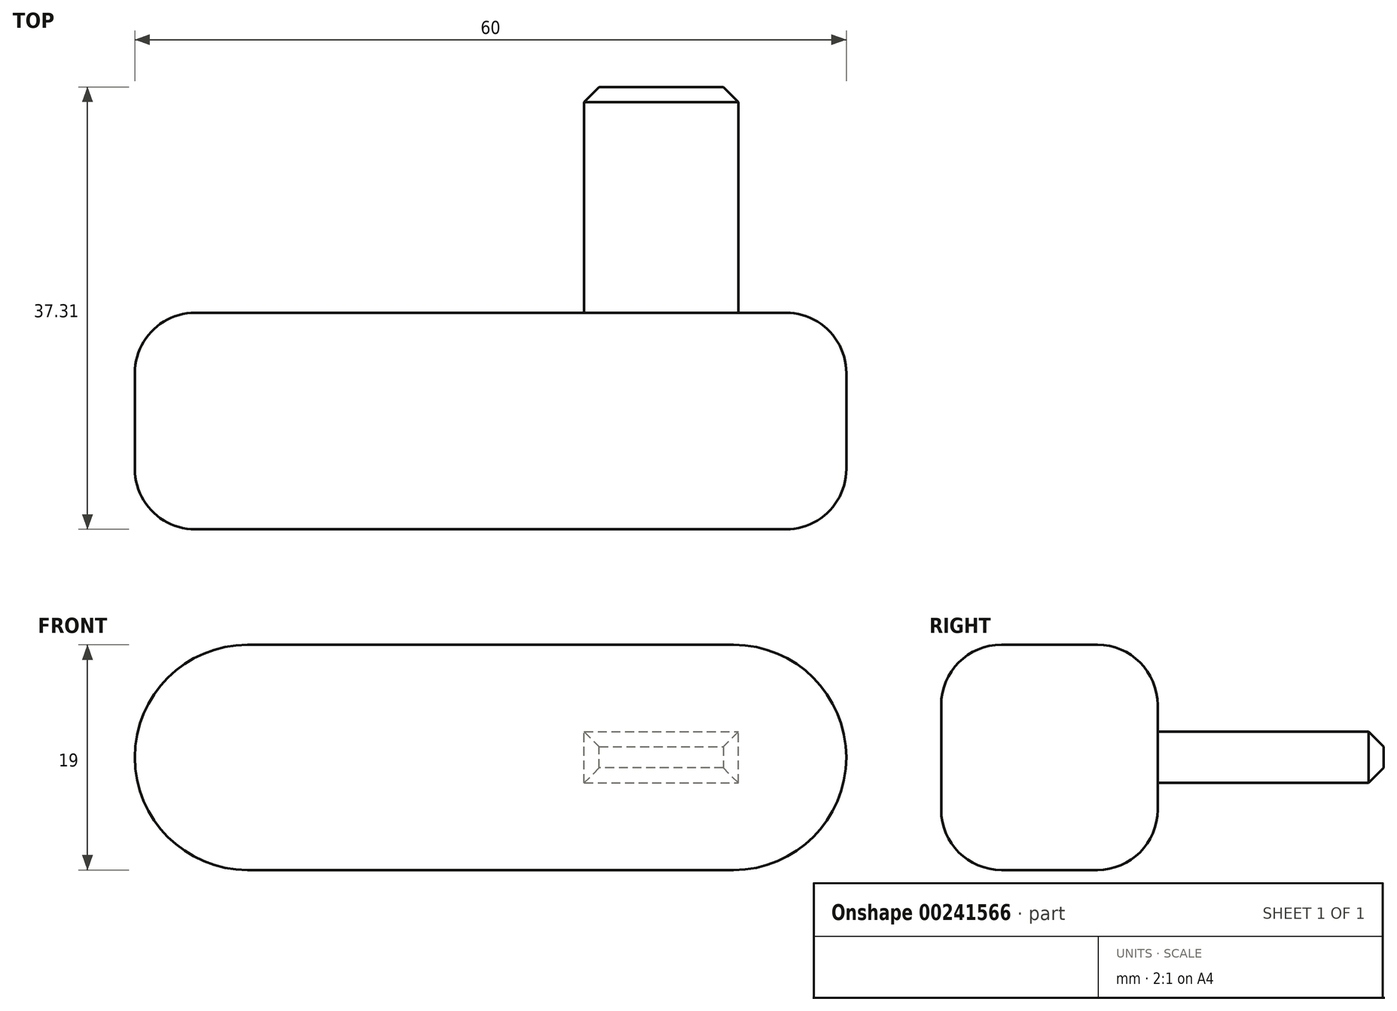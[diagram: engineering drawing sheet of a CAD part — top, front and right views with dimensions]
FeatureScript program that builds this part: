
annotation { "Feature Type Name" : "Feature", "Feature Type Description" : "" }
export const myFeature = defineFeature(function(context is Context, id is Id, definition is map)
    precondition{}
    {
        {
            var Q0;
            Q0=qCreatedBy(makeId("Front.planeOp"),FACE);
            var sketch = newSketch(context, id + "F0", { "sketchPlane" : qUnion([Q0])});
            skLineSegment(sketch, "E0.bottom", {"start": v(-30, 9.5) * mm, "end": v(30, 9.5) * mm});
            skLineSegment(sketch, "E0.top", {"start": v(-30, -9.5) * mm, "end": v(30, -9.5) * mm});
            skLineSegment(sketch, "E0.left", {"start": v(-30, 9.5) * mm, "end": v(-30, -9.5) * mm});
            skLineSegment(sketch, "E0.right", {"start": v(30, 9.5) * mm, "end": v(30, -9.5) * mm});
            skPoint(sketch, "E0.middle", {"position": v(0, 0) * mm});
            skSolve(sketch);
        }
        {
            var Q0;
            Q0=makeQuery(id+"F0.imprint","IMPRINT",FACE,{"disambiguationData":[TD([[makeQuery(id+"F0.imprint","IMPRINT",EDGE,{"derivedFrom":sQuery(id+"F0.wireOp",EDGE,"E0.bottom")}),-1.0]])]});
            extrude(context, id + "F1", {"entities" : qUnion([Q0]), "endBound" : BoundingType.SYMMETRIC, "depth" : 18.26 * mm});
        }
        {
            var Q0;
            Q0=makeQuery(id+"F1.opExtrude","SWEPT_EDGE",EDGE,{"disambiguationData":[OSD([sQuery(id+"F0.wireOp",EDGE,"E0.bottom"),sQuery(id+"F0.wireOp",EDGE,"E0.right")])]});
            var Q1;
            Q1=makeQuery(id+"F1.opExtrude","SWEPT_EDGE",EDGE,{"disambiguationData":[OSD([sQuery(id+"F0.wireOp",EDGE,"E0.top"),sQuery(id+"F0.wireOp",EDGE,"E0.right")])]});
            var Q2;
            Q2=makeQuery(id+"F1.opExtrude","SWEPT_EDGE",EDGE,{"disambiguationData":[OSD([sQuery(id+"F0.wireOp",EDGE,"E0.bottom"),sQuery(id+"F0.wireOp",EDGE,"E0.left")])]});
            var Q3;
            Q3=makeQuery(id+"F1.opExtrude","SWEPT_EDGE",EDGE,{"disambiguationData":[OSD([sQuery(id+"F0.wireOp",EDGE,"E0.top"),sQuery(id+"F0.wireOp",EDGE,"E0.left")])]});
            fillet(context, id + "F2", {"entities" : qUnion([Q0, Q1, Q2, Q3]), "radius" : 19 * mm / 2, "tangentPropagation" : true, "allowEdgeOverflow" : false});
        }
        {
            var Q0;
            Q0=makeQuery(id+"F1.opExtrude","CAP_FACE",FACE,{"disambiguationData":[OSD([sQuery(id+"F0.wireOp",EDGE,"E0.bottom"),sQuery(id+"F0.wireOp",EDGE,"E0.top"),sQuery(id+"F0.wireOp",EDGE,"E0.left"),sQuery(id+"F0.wireOp",EDGE,"E0.right")])],"isStart":true});
            var sketch = newSketch(context, id + "F3", { "sketchPlane" : qUnion([Q0])});
            skLineSegment(sketch, "E1.bottom", {"start": v(-7.9, -2.16) * mm, "end": v(-20.9, -2.16) * mm});
            skLineSegment(sketch, "E1.top", {"start": v(-7.9, 2.16) * mm, "end": v(-20.9, 2.16) * mm});
            skLineSegment(sketch, "E1.left", {"start": v(-7.9, -2.16) * mm, "end": v(-7.9, 2.16) * mm});
            skLineSegment(sketch, "E1.right", {"start": v(-20.9, -2.16) * mm, "end": v(-20.9, 2.16) * mm});
            skPoint(sketch, "E1.middle", {"position": v(-14.4, 0) * mm});
            skSolve(sketch);
        }
        {
            var Q0;
            Q0=makeQuery(id+"F3.imprint","IMPRINT",FACE,{"disambiguationData":[TD([[makeQuery(id+"F3.imprint","IMPRINT",EDGE,{"derivedFrom":sQuery(id+"F3.wireOp",EDGE,"E1.bottom")}),-1.0]])]});
            extrude(context, id + "F4", {"entities" : qUnion([Q0]), "operationType" : NewBodyOperationType.ADD, "depth" : 19.05 * mm});
        }
        {
            var Q0;
            Q0=makeQuery(id+"F4.opExtrude","CAP_EDGE",EDGE,{"disambiguationData":[OSD([sQuery(id+"F3.wireOp",EDGE,"E1.top")])],"isStart":false});
            var Q1;
            Q1=makeQuery(id+"F4.opExtrude","CAP_EDGE",EDGE,{"disambiguationData":[OSD([sQuery(id+"F3.wireOp",EDGE,"E1.right")])],"isStart":false});
            var Q2;
            Q2=makeQuery(id+"F4.opExtrude","CAP_EDGE",EDGE,{"disambiguationData":[OSD([sQuery(id+"F3.wireOp",EDGE,"E1.left")])],"isStart":false});
            var Q3;
            Q3=makeQuery(id+"F4.opExtrude","CAP_EDGE",EDGE,{"disambiguationData":[OSD([sQuery(id+"F3.wireOp",EDGE,"E1.bottom")])],"isStart":false});
            chamfer(context, id + "F5", {"entities" : qUnion([Q0, Q1, Q2, Q3]), "width" : 1.27 * mm, "tangentPropagation" : true});
        }
        {
            var Q0;
            Q0=makeQuery(id+"F1.opExtrude","CAP_EDGE",EDGE,{"disambiguationData":[OSD([sQuery(id+"F0.wireOp",EDGE,"E0.bottom")])],"isStart":true});
            var Q1;
            Q1=makeQuery(id+"F1.opExtrude","CAP_EDGE",EDGE,{"disambiguationData":[OSD([sQuery(id+"F0.wireOp",EDGE,"E0.bottom")])],"isStart":false});
            fillet(context, id + "F6", {"entities" : qUnion([Q0, Q1]), "radius" : 5.08 * mm, "tangentPropagation" : true, "allowEdgeOverflow" : false});
        }
    });
